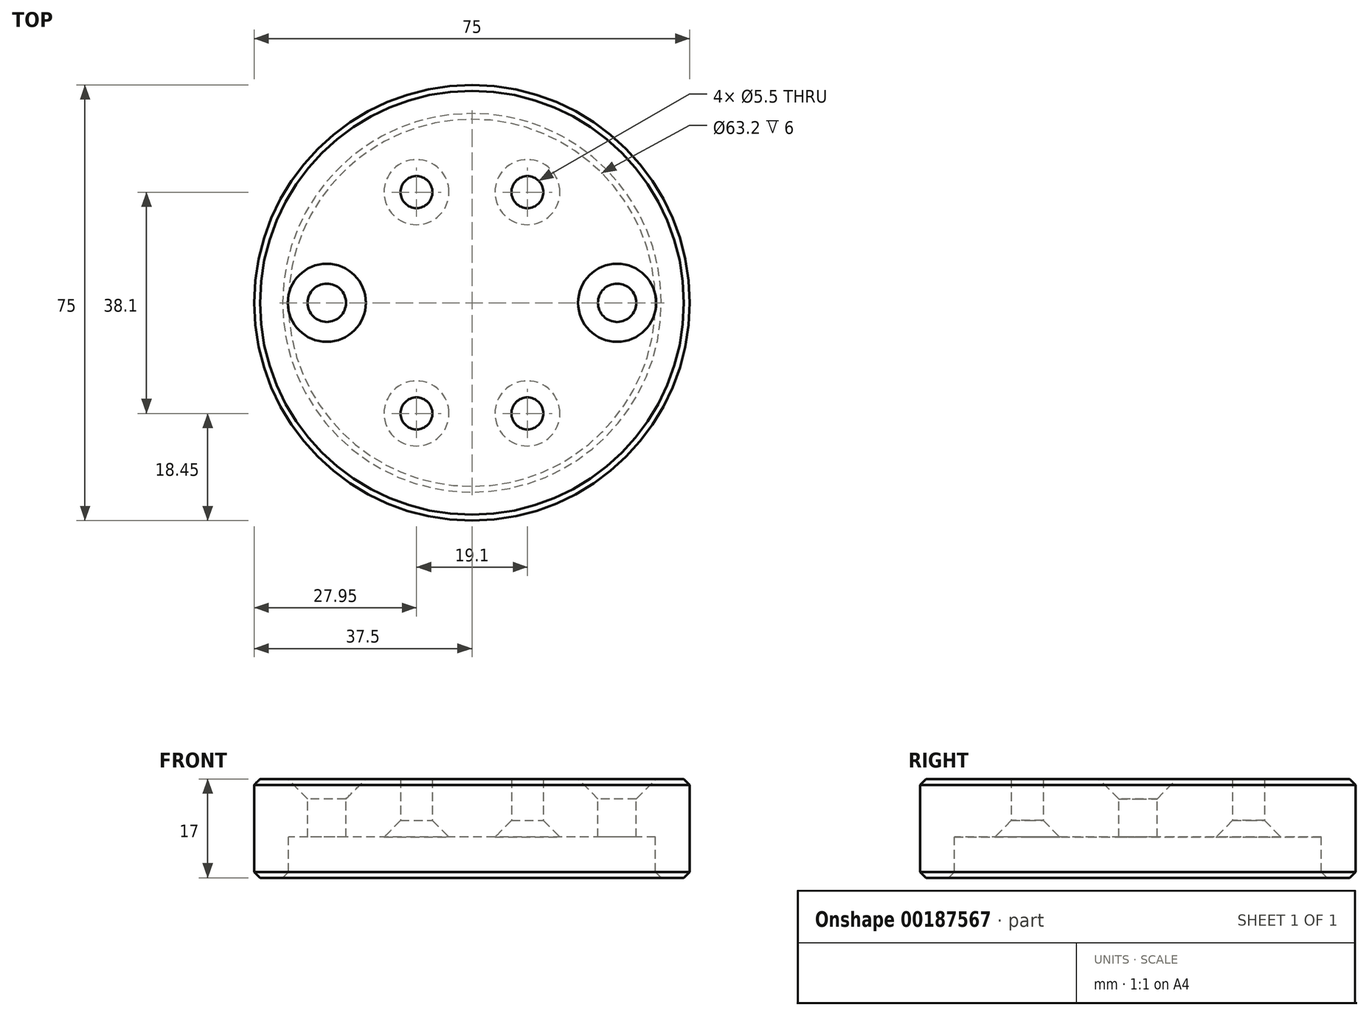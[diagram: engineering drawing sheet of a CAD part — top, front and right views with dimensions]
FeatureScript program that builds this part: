
annotation { "Feature Type Name" : "Feature", "Feature Type Description" : "" }
export const myFeature = defineFeature(function(context is Context, id is Id, definition is map)
    precondition{}
    {
        {
            var Q0;
            Q0=qCreatedBy(makeId("Front.planeOp"),FACE);
            var sketch = newSketch(context, id + "F0", { "sketchPlane" : qUnion([Q0])});
            skLineSegment(sketch, "E0", {"start": v(0, 0) * mm, "end": v(31.6, 0) * mm});
            skLineSegment(sketch, "E1", {"start": v(31.6, 0) * mm, "end": v(31.6, -7) * mm});
            skLineSegment(sketch, "E2", {"start": v(31.6, -7) * mm, "end": v(37.5, -7) * mm});
            skLineSegment(sketch, "E3", {"start": v(37.5, -7) * mm, "end": v(37.5, 10) * mm});
            skLineSegment(sketch, "E4", {"start": v(37.5, 10) * mm, "end": v(0, 10) * mm});
            skLineSegment(sketch, "E5", {"start": v(0, 10) * mm, "end": v(0, 0) * mm});
            skSolve(sketch);
        }
        {
            var Q0;
            Q0 = qSketchRegion(id + "F0", true);
            var Q1;
            Q1=sQuery(id+"F0.wireOp",EDGE,"E5");
            revolve(context, id + "F1", {"entities" : qUnion([Q0]), "axis" : qUnion([Q1]), "revolveType" : RevolveType.FULL});
        }
        {
            var Q0;
            Q0=makeQuery(id+"F1.opRevolve","SWEPT_EDGE",EDGE,{"disambiguationData":[OSD([sQuery(id+"F0.wireOp",EDGE,"E1"),sQuery(id+"F0.wireOp",EDGE,"E2")])]});
            var Q1;
            Q1=makeQuery(id+"F1.opRevolve","SWEPT_EDGE",EDGE,{"disambiguationData":[OSD([sQuery(id+"F0.wireOp",EDGE,"E2"),sQuery(id+"F0.wireOp",EDGE,"E3")])]});
            var Q2;
            Q2=makeQuery(id+"F1.opRevolve","SWEPT_EDGE",EDGE,{"disambiguationData":[OSD([sQuery(id+"F0.wireOp",EDGE,"E3"),sQuery(id+"F0.wireOp",EDGE,"E4")])]});
            chamfer(context, id + "F2", {"entities" : qUnion([Q0, Q1, Q2]), "width" : 1 * mm, "tangentPropagation" : true});
        }
        {
            var Q0;
            Q0=makeQuery(id+"F1.opRevolve","SWEPT_FACE",FACE,{"disambiguationData":[OSD([sQuery(id+"F0.wireOp",EDGE,"E4")])]});
            var sketch = newSketch(context, id + "F3", { "sketchPlane" : qUnion([Q0])});
            skCircle(sketch, "E6", {"center": v(0, 0) * mm, "radius": 25 * mm, "construction": true});
            skPoint(sketch, "E7", {"position": v(-25, 0) * mm});
            skPoint(sketch, "E8", {"position": v(25, 0) * mm});
            skSolve(sketch);
        }
        {
            var Q0;
            Q0=sQuery(id+"F3.wireOp",VERTEX,"E7");
            var Q1;
            Q1=sQuery(id+"F3.wireOp",VERTEX,"E8");
            var Q2;
            Q2=makeQuery(id+"F1.opRevolve","SWEPT_BODY",BODY,{"disambiguationData":[OSD([sQuery(id+"F0.wireOp",EDGE,"E0"),sQuery(id+"F0.wireOp",EDGE,"E1"),sQuery(id+"F0.wireOp",EDGE,"E2"),sQuery(id+"F0.wireOp",EDGE,"E3"),sQuery(id+"F0.wireOp",EDGE,"E4"),sQuery(id+"F0.wireOp",EDGE,"E5")])]});
            hole(context, id + "F4", {"style" : HoleStyle.C_SINK, "endStyle" : HoleEndStyle.THROUGH, "standardTappedOrClearance" : lookupTablePath({ "standard" : "ISO", "fit" : "Normal", "size" : "M6", "type" : "Clearance" }), "standardBlindInLast" : lookupTablePath({ "fit" : "Standard", "standard" : "ISO", "size" : "M6", "type" : "Clearance" }), "holeDiameter" : 6.6 * mm, "cSinkDiameter" : 13.44 * mm, "cSinkAngle" : 90 * degree, "locations" : qUnion([Q0, Q1]), "scope" : qUnion([Q2]), "isTappedThrough" : true});
        }
        {
            var Q0;
            Q0=makeQuery(id+"F1.opRevolve","SWEPT_FACE",FACE,{"disambiguationData":[OSD([sQuery(id+"F0.wireOp",EDGE,"E0")])]});
            var sketch = newSketch(context, id + "F5", { "sketchPlane" : qUnion([Q0])});
            skLineSegment(sketch, "E9", {"start": v(0, 0) * mm, "end": v(9.55, 0) * mm, "construction": true});
            skLineSegment(sketch, "E10", {"start": v(9.55, 0) * mm, "end": v(9.55, 19.05) * mm, "construction": true});
            skLineSegment(sketch, "E11", {"start": v(9.55, 19.05) * mm, "end": v(-9.55, 19.05) * mm, "construction": true});
            skLineSegment(sketch, "E12", {"start": v(-9.55, 19.05) * mm, "end": v(-9.55, -19.05) * mm, "construction": true});
            skLineSegment(sketch, "E13", {"start": v(-9.55, -19.05) * mm, "end": v(9.55, -19.05) * mm, "construction": true});
            skPoint(sketch, "E14", {"position": v(-9.55, 19.05) * mm});
            skPoint(sketch, "E15", {"position": v(9.55, 19.05) * mm});
            skPoint(sketch, "E16", {"position": v(9.55, -19.05) * mm});
            skPoint(sketch, "E17", {"position": v(-9.55, -19.05) * mm});
            skSolve(sketch);
        }
        {
            var Q0;
            Q0=sQuery(id+"F5.wireOp",VERTEX,"E14");
            var Q1;
            Q1=sQuery(id+"F5.wireOp",VERTEX,"E15");
            var Q2;
            Q2=sQuery(id+"F5.wireOp",VERTEX,"E16");
            var Q3;
            Q3=sQuery(id+"F5.wireOp",VERTEX,"E17");
            var Q4;
            Q4=makeQuery(id+"F1.opRevolve","SWEPT_BODY",BODY,{"disambiguationData":[OSD([sQuery(id+"F0.wireOp",EDGE,"E0"),sQuery(id+"F0.wireOp",EDGE,"E1"),sQuery(id+"F0.wireOp",EDGE,"E2"),sQuery(id+"F0.wireOp",EDGE,"E3"),sQuery(id+"F0.wireOp",EDGE,"E4"),sQuery(id+"F0.wireOp",EDGE,"E5")])]});
            hole(context, id + "F6", {"style" : HoleStyle.C_SINK, "endStyle" : HoleEndStyle.THROUGH, "standardTappedOrClearance" : lookupTablePath({ "standard" : "ISO", "fit" : "Normal", "size" : "M5", "type" : "Clearance" }), "standardBlindInLast" : lookupTablePath({ "fit" : "Standard", "standard" : "ISO", "size" : "M5", "type" : "Clearance" }), "holeDiameter" : 5.5 * mm, "cSinkDiameter" : 11.2 * mm, "cSinkAngle" : 90 * degree, "locations" : qUnion([Q0, Q1, Q2, Q3]), "scope" : qUnion([Q4]), "isTappedThrough" : true});
        }
    });
